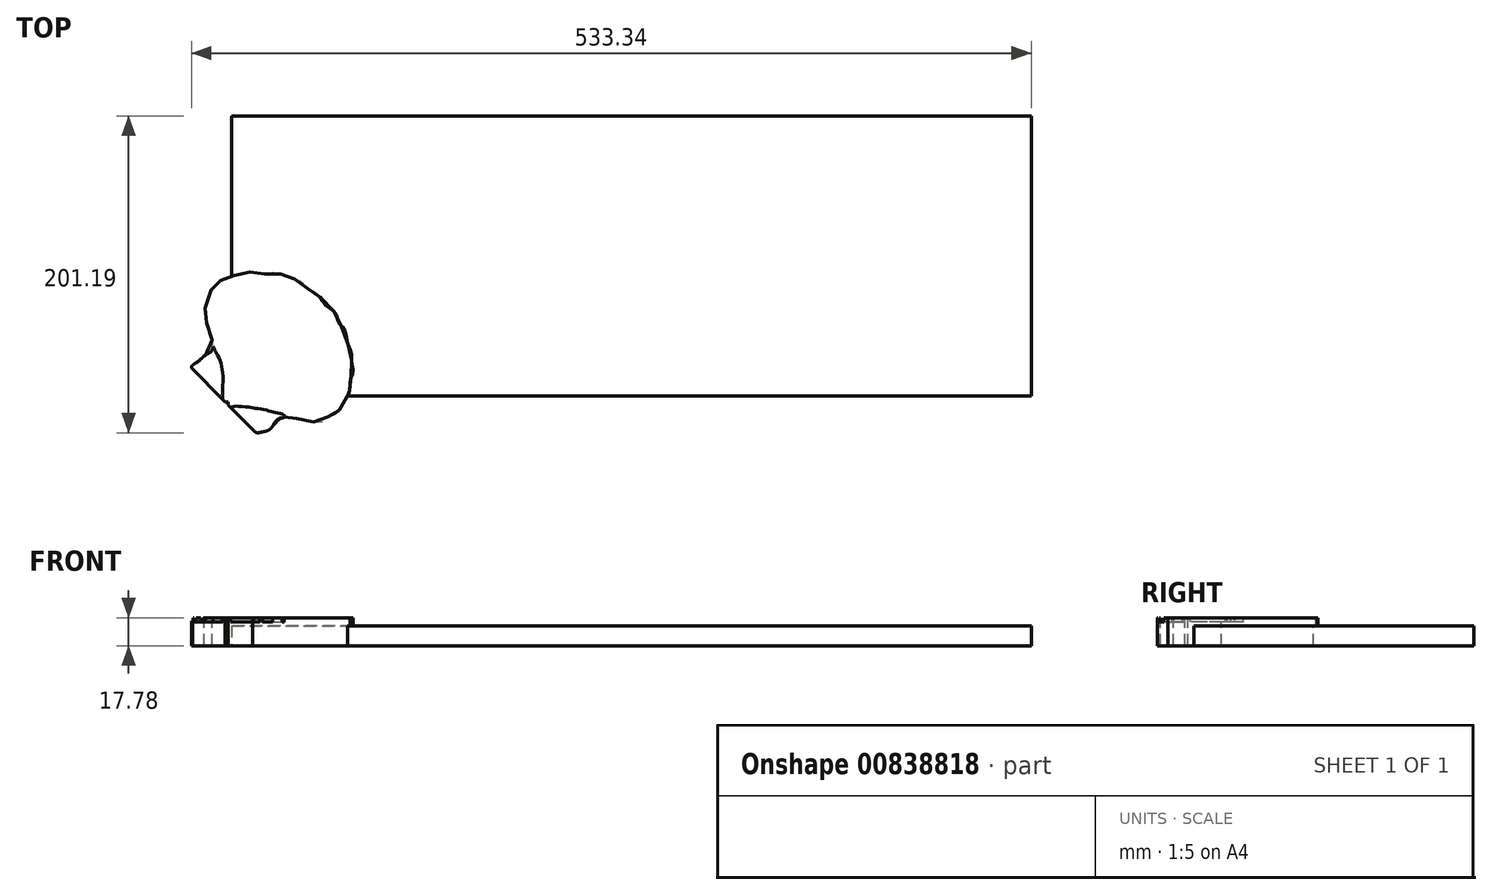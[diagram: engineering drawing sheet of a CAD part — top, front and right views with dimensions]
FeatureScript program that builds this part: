
annotation { "Feature Type Name" : "Feature", "Feature Type Description" : "" }
export const myFeature = defineFeature(function(context is Context, id is Id, definition is map)
    precondition{}
    {
        {
            var Q0;
            Q0=qCreatedBy(makeId("Top.planeOp"),FACE);
            var sketch = newSketch(context, id + "F0", { "sketchPlane" : qUnion([Q0])});
            skLineSegment(sketch, "E0.bottom", {"start": v(-254, 88.9) * mm, "end": v(254, 88.9) * mm});
            skLineSegment(sketch, "E0.top", {"start": v(-254, -88.9) * mm, "end": v(254, -88.9) * mm});
            skLineSegment(sketch, "E0.left", {"start": v(-254, 88.9) * mm, "end": v(-254, -88.9) * mm});
            skLineSegment(sketch, "E0.right", {"start": v(254, 88.9) * mm, "end": v(254, -88.9) * mm});
            skPoint(sketch, "E1", {"position": v(0, 88.9) * mm});
            skPoint(sketch, "E2", {"position": v(-254, 0) * mm});
            skPoint(sketch, "E3", {"position": v(0, 0) * mm});
            skSolve(sketch);
        }
        {
            var Q0;
            Q0 = qSketchRegion(id + "F0", true);
            extrude(context, id + "F1", {"entities" : qUnion([Q0]), "depth" : 12.7 * mm, "offsetDistance" : 25.4 * mm});
        }
        {
            var Q0;
            Q0=makeQuery(id+"F1.opExtrude","CAP_FACE",FACE,{"disambiguationData":[OSD([sQuery(id+"F0.wireOp",EDGE,"E0.bottom"),sQuery(id+"F0.wireOp",EDGE,"E0.top"),sQuery(id+"F0.wireOp",EDGE,"E0.left"),sQuery(id+"F0.wireOp",EDGE,"E0.right")])],"isStart":false});
            var sketch = newSketch(context, id + "F2", { "sketchPlane" : qUnion([Q0])});
            skPoint(sketch, "E4", {"position": v(-261.62, -96.52) * mm});
            skLineSegment(sketch, "E5", {"start": v(-254, -88.9) * mm, "end": v(-254, -113.39) * mm, "construction": true});
            skLineSegment(sketch, "E6", {"start": v(-254, -88.9) * mm, "end": v(-303.59, -88.9) * mm, "construction": true});
            skPoint(sketch, "E7", {"position": v(-254, -104.14) * mm});
            skPoint(sketch, "E8", {"position": v(-269.24, -88.9) * mm});
            skSolve(sketch);
        }
        {
            var Q0;
            Q0=makeQuery(id+"F2.imprint","IMPRINT",FACE,{"disambiguationData":[TD([[makeQuery(id+"F2.imprint","IMPRINT",EDGE,{"derivedFrom":makeQuery(id+"F1.opExtrude","CAP_EDGE",EDGE,{"disambiguationData":[OSD([sQuery(id+"F0.wireOp",EDGE,"E0.bottom")])],"isStart":false})}),-1.0]])]});
            var sketch = newSketch(context, id + "F3", { "sketchPlane" : qUnion([Q0])});
            skLineSegment(sketch, "E9", {"start": v(-278.58, -71.63) * mm, "end": v(-258.1, -92.75) * mm});
            skLineSegment(sketch, "E10", {"start": v(-258.1, -92.75) * mm, "end": v(-255.95, -92.75) * mm});
            skLineSegment(sketch, "E11", {"start": v(-255.95, -92.75) * mm, "end": v(-255.95, -94.63) * mm});
            skLineSegment(sketch, "E12", {"start": v(-255.95, -94.63) * mm, "end": v(-240.44, -110.27) * mm});
            skFitSpline(sketch, "E13", {"points": [v(-240.44, -110.27) * mm, v(-238.17, -112.16) * mm, v(-235.34, -111.97) * mm, v(-229.86, -110.27) * mm, v(-226.65, -106.68) * mm, v(-222.5, -103.1) * mm, v(-221.18, -102.72) * mm, v(-219.86, -101.96) * mm, v(-217.97, -101.96) * mm, v(-212.68, -103.1) * mm, v(-207.02, -104.42) * mm, v(-200.22, -105.36) * mm, v(-194.56, -104.42) * mm, v(-192.3, -101.77) * mm, v(-189.08, -101.02) * mm, v(-185.68, -98) * mm, v(-181.53, -91.95) * mm, v(-178.5, -83.08) * mm, v(-178.7, -79.5) * mm, v(-176.8, -74.02) * mm, v(-177.56, -67.22) * mm, v(-178.13, -60.04) * mm, v(-180.02, -56.27) * mm, v(-182.28, -46.45) * mm, v(-186.06, -42.1) * mm, v(-187.95, -36.06) * mm, v(-193.8, -31.53) * mm, v(-197.95, -25.68) * mm, v(-202.69, -22.38) * mm, v(-206.33, -19.94) * mm, v(-210.52, -16.03) * mm, v(-216.2, -14) * mm, v(-220.25, -12.79) * mm, v(-224.3, -11.03) * mm, v(-230.65, -10.9) * mm, v(-234.7, -11.43) * mm, v(-239.02, -10.22) * mm, v(-244.56, -10.62) * mm, v(-250.37, -11.7) * mm, v(-254.69, -13.33) * mm, v(-259, -14.54) * mm, v(-262.25, -16.84) * mm, v(-265.09, -19.27) * mm, v(-267.52, -22.51) * mm, v(-269.95, -30.07) * mm, v(-271.44, -36.56) * mm, v(-270.5, -40.74) * mm, v(-267.52, -48.3) * mm, v(-266.17, -53.44) * mm, v(-267.25, -59.52) * mm, v(-271.44, -63.7) * mm, v(-275.22, -66.95) * mm, v(-277.27, -68.3) * mm, v(-278.08, -68.88) * mm, v(-278.58, -69.24) * mm, v(-278.58, -71.63) * mm], "startDerivative": vector(154.3, -169.55) * mm, "endDerivative": vector(340.75, -198.77) * mm});
            skSolve(sketch);
        }
        {
            var Q0;
            Q0 = qSketchRegion(id + "F3", true);
            extrude(context, id + "F4", {"entities" : qUnion([Q0]), "operationType" : NewBodyOperationType.ADD, "oppositeDirection" : true, "depth" : 12.7 * mm, "offsetDistance" : 25.4 * mm, "hasSecondDirection" : true, "secondDirectionOppositeDirection" : false, "secondDirectionDepth" : 5.08 * mm});
        }
        {
            var Q0;
            Q0=makeQuery(id+"F4.opExtrude","CAP_FACE",FACE,{"disambiguationData":[OSD([sQuery(id+"F3.wireOp",EDGE,"E9"),sQuery(id+"F3.wireOp",EDGE,"E10"),sQuery(id+"F3.wireOp",EDGE,"E11"),sQuery(id+"F3.wireOp",EDGE,"E12"),sQuery(id+"F3.wireOp",EDGE,"E13")])],"isStart":true});
            var sketch = newSketch(context, id + "F5", { "sketchPlane" : qUnion([Q0])});
            skFitSpline(sketch, "E14", {"points": [v(-266.23, -56.2) * mm, v(-264.69, -59.35) * mm, v(-262.54, -63.44) * mm, v(-259.81, -71.82) * mm, v(-259.42, -81.37) * mm, v(-259.62, -87.02) * mm, v(-259.72, -88.97) * mm, v(-259.58, -91.22) * mm], "startDerivative": vector(12.29, -25.89) * mm, "endDerivative": vector(-5.79, -30.21) * mm});
            skFitSpline(sketch, "E15", {"points": [v(-219.64, -101.9) * mm, v(-222.2, -100.27) * mm, v(-227.07, -99.1) * mm, v(-231.55, -97.94) * mm, v(-237.98, -96.77) * mm, v(-243.44, -95.99) * mm, v(-251.43, -95.4) * mm, v(-254.48, -96.1) * mm], "startDerivative": vector(-20.19, 15.95) * mm, "endDerivative": vector(-22.74, -8.16) * mm});
            skLineSegment(sketch, "E16.0", {"start": v(-278.58, -71.63) * mm, "end": v(-259.58, -91.22) * mm});
            skFitSpline(sketch, "E16.1", {"points": [v(-240.44, -110.27) * mm, v(-239.7, -111.07) * mm, v(-238.26, -112.66) * mm, v(-235.3, -111.9) * mm, v(-229.24, -110.84) * mm, v(-227.1, -106.68) * mm, v(-222.7, -102.78) * mm, v(-221.18, -102.92) * mm, v(-219.84, -101.7) * mm, v(-217.82, -101.93) * mm, v(-212.44, -103.12) * mm, v(-207.04, -104.5) * mm, v(-200.48, -105.57) * mm, v(-194.1, -105.34) * mm, v(-192.76, -101.05) * mm, v(-188.68, -101.61) * mm, v(-185.44, -97.76) * mm, v(-181.25, -92.38) * mm, v(-177.73, -83.14) * mm, v(-179.47, -79.51) * mm, v(-175.7, -73.86) * mm, v(-178.12, -67.46) * mm, v(-177.36, -59.66) * mm, v(-180.87, -56.75) * mm, v(-180.9, -45.51) * mm, v(-187.13, -42.9) * mm, v(-186.61, -35.01) * mm, v(-194.72, -32.34) * mm, v(-197.24, -25.18) * mm, v(-202.72, -22.4) * mm, v(-206.54, -20.21) * mm, v(-210.13, -15.4) * mm, v(-216.17, -14.02) * mm, v(-220.33, -13) * mm, v(-224.14, -10.5) * mm, v(-230.7, -10.6) * mm, v(-234.68, -12.04) * mm, v(-239.06, -9.59) * mm, v(-244.56, -10.72) * mm, v(-250.43, -11.38) * mm, v(-254.53, -13.57) * mm, v(-259.18, -14.14) * mm, v(-262.22, -16.86) * mm, v(-265.22, -19.23) * mm, v(-267.98, -22.42) * mm, v(-269.84, -30.06) * mm, v(-271.97, -36.57) * mm, v(-270.56, -40.73) * mm, v(-267.4, -48.42) * mm, v(-265.79, -53.2) * mm, v(-266.5, -60.05) * mm, v(-271.46, -63.52) * mm, v(-274.98, -66.98) * mm, v(-277.2, -68.19) * mm, v(-278.1, -68.93) * mm, v(-278.55, -69.11) * mm, v(-280.03, -70.78) * mm, v(-278.58, -71.63) * mm]});
            skLineSegment(sketch, "E16.2", {"start": v(-254.48, -96.1) * mm, "end": v(-240.44, -110.27) * mm});
            skFitSpline(sketch, "E17.trimOffspring", {"points": [v(-240.44, -110.27) * mm, v(-239.7, -111.07) * mm, v(-238.26, -112.66) * mm, v(-235.3, -111.9) * mm, v(-229.24, -110.84) * mm, v(-227.1, -106.68) * mm, v(-222.7, -102.78) * mm, v(-221.18, -102.92) * mm, v(-219.84, -101.7) * mm, v(-217.82, -101.93) * mm, v(-212.44, -103.12) * mm, v(-207.04, -104.5) * mm, v(-200.48, -105.57) * mm, v(-194.1, -105.34) * mm, v(-192.76, -101.05) * mm, v(-188.68, -101.61) * mm, v(-185.44, -97.76) * mm, v(-181.25, -92.38) * mm, v(-177.73, -83.14) * mm, v(-179.47, -79.51) * mm, v(-175.7, -73.86) * mm, v(-178.12, -67.46) * mm, v(-177.36, -59.66) * mm, v(-180.87, -56.75) * mm, v(-180.9, -45.51) * mm, v(-187.13, -42.9) * mm, v(-186.61, -35.01) * mm, v(-194.72, -32.34) * mm, v(-197.24, -25.18) * mm, v(-202.72, -22.4) * mm, v(-206.54, -20.21) * mm, v(-210.13, -15.4) * mm, v(-216.17, -14.02) * mm, v(-220.33, -13) * mm, v(-224.14, -10.5) * mm, v(-230.7, -10.6) * mm, v(-234.68, -12.04) * mm, v(-239.06, -9.59) * mm, v(-244.56, -10.72) * mm, v(-250.43, -11.38) * mm, v(-254.53, -13.57) * mm, v(-259.18, -14.14) * mm, v(-262.22, -16.86) * mm, v(-265.22, -19.23) * mm, v(-267.98, -22.42) * mm, v(-269.84, -30.06) * mm, v(-271.97, -36.57) * mm, v(-270.56, -40.73) * mm, v(-267.4, -48.42) * mm, v(-265.79, -53.2) * mm, v(-266.5, -60.05) * mm, v(-271.46, -63.52) * mm, v(-274.98, -66.98) * mm, v(-277.2, -68.19) * mm, v(-278.1, -68.93) * mm, v(-278.55, -69.11) * mm, v(-280.03, -70.78) * mm, v(-278.58, -71.63) * mm]});
            skSolve(sketch);
        }
        {
            var Q0;
            Q0 = qSketchRegion(id + "F5", true);
            extrude(context, id + "F6", {"entities" : qUnion([Q0]), "operationType" : NewBodyOperationType.REMOVE, "oppositeDirection" : true, "depth" : 2.54 * mm, "offsetDistance" : 25.4 * mm});
        }
    });
